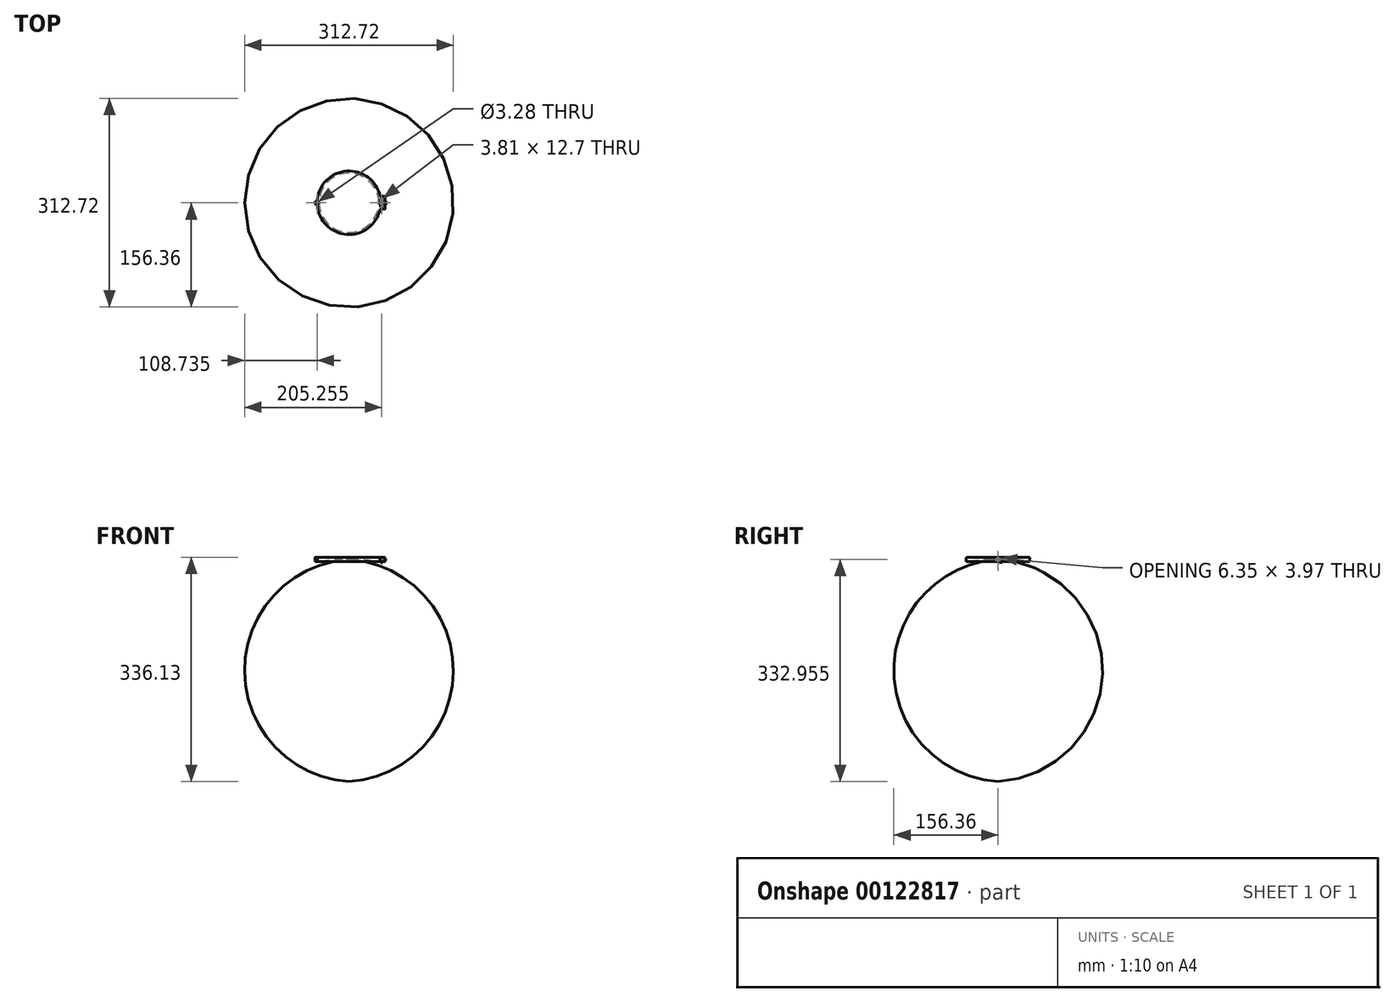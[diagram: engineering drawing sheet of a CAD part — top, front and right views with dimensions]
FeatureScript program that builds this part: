
annotation { "Feature Type Name" : "Feature", "Feature Type Description" : "" }
export const myFeature = defineFeature(function(context is Context, id is Id, definition is map)
    precondition{}
    {
        {
            var Q0;
            Q0=qCreatedBy(makeId("Front.planeOp"),FACE);
            var sketch = newSketch(context, id + "F0", { "sketchPlane" : qUnion([Q0])});
            skLineSegment(sketch, "E0", {"start": v(0, 0) * mm, "end": v(47.63, 0) * mm});
            skLineSegment(sketch, "E1", {"start": v(47.63, 0) * mm, "end": v(47.63, 6.35) * mm});
            skLineSegment(sketch, "E2", {"start": v(47.63, 6.35) * mm, "end": v(44.45, 6.35) * mm});
            skLineSegment(sketch, "E3", {"start": v(44.45, 6.35) * mm, "end": v(44.45, 6.35) * mm});
            skLineSegment(sketch, "E4", {"start": v(0, 3.17) * mm, "end": v(0, 0) * mm});
            skPoint(sketch, "E5.1.internal.snap0", {"position": v(0, 3.17) * mm});
            skArc(sketch, "E6", {"start": v(0, 3.17) * mm, "mid": v(22.33, 3.27) * mm, "end": v(44.45, 6.35) * mm});
            skPoint(sketch, "E7.orphan", {"position": v(0, 6.35) * mm});
            skSolve(sketch);
        }
        {
            var Q0;
            Q0=makeQuery(id+"F0.imprint","IMPRINT",FACE,{"disambiguationData":[TD([[makeQuery(id+"F0.imprint","IMPRINT",EDGE,{"derivedFrom":sQuery(id+"F0.wireOp",EDGE,"E0")}),1.0]])]});
            var Q1;
            Q1=sQuery(id+"F0.wireOp",EDGE,"E4");
            revolve(context, id + "F1", {"entities" : qUnion([Q0]), "axis" : qUnion([Q1]), "revolveType" : RevolveType.FULL});
        }
        {
            var Q0;
            Q0=makeQuery(id+"F1.opRevolve","SWEPT_BODY",BODY,{"disambiguationData":[OSD([sQuery(id+"F0.wireOp",EDGE,"E0"),sQuery(id+"F0.wireOp",EDGE,"E1"),sQuery(id+"F0.wireOp",EDGE,"E2"),sQuery(id+"F0.wireOp",EDGE,"E3"),sQuery(id+"F0.wireOp",EDGE,"8306908f-6550-4d79-8b0d-f81cb6d910f5"),sQuery(id+"F0.wireOp",EDGE,"E4")])]});
            var Q1;
            Q1=qCreatedBy(makeId("Top.planeOp"),FACE);
            mirror(context, id + "F2", {"entities" : qUnion([Q0]), "mirrorPlane" : qUnion([Q1])});
        }
        {
            var Q0;
            Q0=makeQuery(id+"F1.opRevolve","SWEPT_BODY",BODY,{"disambiguationData":[OSD([sQuery(id+"F0.wireOp",EDGE,"E0"),sQuery(id+"F0.wireOp",EDGE,"E1"),sQuery(id+"F0.wireOp",EDGE,"E2"),sQuery(id+"F0.wireOp",EDGE,"E3"),sQuery(id+"F0.wireOp",EDGE,"8306908f-6550-4d79-8b0d-f81cb6d910f5"),sQuery(id+"F0.wireOp",EDGE,"E4")])]});
            deleteBodies(context, id + "F3", {"entities" : qUnion([Q0])});
        }
        {
            var Q0;
            Q0=makeQuery(id+"F2.opPattern","COPY",FACE,{"derivedFrom":makeQuery(id+"F1.opRevolve","SWEPT_FACE",FACE,{"disambiguationData":[OSD([sQuery(id+"F0.wireOp",EDGE,"E0")])]}),"instanceName":"1"});
            var sketch = newSketch(context, id + "F4", { "sketchPlane" : qUnion([Q0])});
            skCircle(sketch, "E8", {"center": v(-47.63, 0) * mm, "radius": 3.18 * mm});
            skSolve(sketch);
        }
        {
            var Q0;
            {var subQ0=sQuery(id+"F4.wireOp",EDGE,"E8");var subQ1=makeQuery(id+"F2.opPattern","COPY",EDGE,{"derivedFrom":makeQuery(id+"F1.opRevolve","SWEPT_EDGE",EDGE,{"disambiguationData":[OSD([sQuery(id+"F0.wireOp",EDGE,"E0"),sQuery(id+"F0.wireOp",EDGE,"E1")])]}),"instanceName":"1"});var subQ2=makeQuery(id+"F4.imprint","INTERSECT",VERTEX,{"disambiguationData":[OD(0.0)],"derivedFrom":[subQ1,subQ0]});Q0=makeQuery(id+"F4.imprint","IMPRINT",FACE,{"disambiguationData":[TD([[makeQuery(id+"F4.imprint","IMPRINT",EDGE,{"disambiguationData":[TD([[subQ2,1.0]])],"derivedFrom":subQ0}),1.0]])]});}
            var Q1;
            Q1=makeQuery(id+"F2.opPattern","COPY",FACE,{"derivedFrom":makeQuery(id+"F1.opRevolve","SWEPT_FACE",FACE,{"disambiguationData":[OSD([sQuery(id+"F0.wireOp",EDGE,"E2")])]}),"instanceName":"1"});
            extrude(context, id + "F5", {"entities" : qUnion([Q0]), "operationType" : NewBodyOperationType.ADD, "endBound" : BoundingType.UP_TO_SURFACE, "oppositeDirection" : true, "endBoundEntityFace" : qUnion([Q1]), "depth" : 25.4 * mm});
        }
        {
            var Q0;
            Q0=qCreatedBy(makeId("Front.planeOp"),FACE);
            var sketch = newSketch(context, id + "F6", { "sketchPlane" : qUnion([Q0])});
            skCircle(sketch, "E9", {"center": v(46.04, -6.35) * mm, "radius": 0.8 * mm});
            skLineSegment(sketch, "E10", {"start": v(45.24, -6.35) * mm, "end": v(46.83, -6.35) * mm});
            skSolve(sketch);
        }
        {
            var Q0;
            {var subQ0=sQuery(id+"F6.wireOp",EDGE,"E10");Q0=makeQuery(id+"F6.imprint","IMPRINT",FACE,{"disambiguationData":[TD([[makeQuery(id+"F6.imprint","IMPRINT",EDGE,{"derivedFrom":subQ0}),-1.0]])]});}
            var Q1;
            Q1=sQuery(id+"F6.wireOp",EDGE,"E10");
            revolve(context, id + "F7", {"operationType" : NewBodyOperationType.REMOVE, "entities" : qUnion([Q0]), "axis" : qUnion([Q1]), "revolveType" : RevolveType.FULL, "oppositeDirection" : true});
        }
        {
            var Q0;
            {var subQ0=sQuery(id+"F0.wireOp",EDGE,"E0");Q0=makeQuery(id+"F5.boolean.opBoolean","MERGE",FACE,{"derivedFrom":[makeQuery(id+"F2.opPattern","COPY",FACE,{"derivedFrom":makeQuery(id+"F1.opRevolve","SWEPT_FACE",FACE,{"disambiguationData":[OSD([subQ0])]}),"instanceName":"1"}),makeQuery(id+"F5.opExtrude","CAP_FACE",FACE,{"disambiguationData":[OSD([subQ0,sQuery(id+"F0.wireOp",EDGE,"E1"),sQuery(id+"F4.wireOp",EDGE,"E8")])],"isStart":true})]});}
            var sketch = newSketch(context, id + "F8", { "sketchPlane" : qUnion([Q0])});
            skPoint(sketch, "E11", {"position": v(-47.63, 0) * mm});
            skSolve(sketch);
        }
        {
            var Q0;
            Q0=sQuery(id+"F8.wireOp",VERTEX,"E11");
            var Q1;
            Q1=makeQuery(id+"F2.opPattern","COPY",BODY,{"derivedFrom":makeQuery(id+"F1.opRevolve","SWEPT_BODY",BODY,{"disambiguationData":[OSD([sQuery(id+"F0.wireOp",EDGE,"E0"),sQuery(id+"F0.wireOp",EDGE,"E1"),sQuery(id+"F0.wireOp",EDGE,"E2"),sQuery(id+"F0.wireOp",EDGE,"E3"),sQuery(id+"F0.wireOp",EDGE,"8306908f-6550-4d79-8b0d-f81cb6d910f5"),sQuery(id+"F0.wireOp",EDGE,"E4")])]}),"instanceName":"1"});
            hole(context, id + "F9", {"style" : HoleStyle.C_SINK, "endStyle" : HoleEndStyle.THROUGH, "holeDiameter" : 3.28 * mm, "cSinkDiameter" : 3.97 * mm, "cSinkAngle" : 90 * degree, "startFromSketch" : true, "locations" : qUnion([Q0]), "scope" : qUnion([Q1]), "isTappedThrough" : true});
        }
        {
            var Q0;
            {var subQ0=sQuery(id+"F0.wireOp",EDGE,"E0");Q0=makeQuery(id+"F5.boolean.opBoolean","MERGE",FACE,{"derivedFrom":[makeQuery(id+"F2.opPattern","COPY",FACE,{"derivedFrom":makeQuery(id+"F1.opRevolve","SWEPT_FACE",FACE,{"disambiguationData":[OSD([subQ0])]}),"instanceName":"1"}),makeQuery(id+"F5.opExtrude","CAP_FACE",FACE,{"disambiguationData":[OSD([subQ0,sQuery(id+"F0.wireOp",EDGE,"E1"),sQuery(id+"F4.wireOp",EDGE,"E8")])],"isStart":true})]});}
            var sketch = newSketch(context, id + "F10", { "sketchPlane" : qUnion([Q0])});
            skLineSegment(sketch, "E12.bottom", {"start": v(53.98, 9.53) * mm, "end": v(41.28, 9.53) * mm});
            skLineSegment(sketch, "E12.top", {"start": v(53.98, -9.52) * mm, "end": v(41.28, -9.52) * mm});
            skLineSegment(sketch, "E12.left", {"start": v(53.98, 9.52) * mm, "end": v(53.98, -9.53) * mm});
            skLineSegment(sketch, "E12.right", {"start": v(41.28, 9.52) * mm, "end": v(41.28, -9.53) * mm});
            skPoint(sketch, "E12.middle", {"position": v(47.63, 0) * mm});
            skLineSegment(sketch, "E13.bottom", {"start": v(50.8, 6.35) * mm, "end": v(47, 6.35) * mm});
            skLineSegment(sketch, "E13.top", {"start": v(50.8, -6.35) * mm, "end": v(47, -6.35) * mm});
            skLineSegment(sketch, "E13.left", {"start": v(50.8, 6.35) * mm, "end": v(50.8, -6.35) * mm});
            skLineSegment(sketch, "E14", {"start": v(47, 6.35) * mm, "end": v(47, -6.35) * mm});
            skPoint(sketch, "E15.orphan", {"position": v(44.45, 6.35) * mm});
            skPoint(sketch, "E16.orphan", {"position": v(44.45, -6.35) * mm});
            skSolve(sketch);
        }
        {
            var Q0;
            {var subQ4=sQuery(id+"F10.wireOp",EDGE,"E12.left");Q0=makeQuery(id+"F10.imprint","IMPRINT",FACE,{"disambiguationData":[TD([[makeQuery(id+"F10.imprint","IMPRINT",EDGE,{"derivedFrom":subQ4}),-1.0]])]});}
            var Q1;
            {var subQ0=sQuery(id+"F0.wireOp",EDGE,"E2");Q1=makeQuery(id+"F5.boolean.opBoolean","MERGE",FACE,{"derivedFrom":[makeQuery(id+"F2.opPattern","COPY",FACE,{"derivedFrom":makeQuery(id+"F1.opRevolve","SWEPT_FACE",FACE,{"disambiguationData":[OSD([subQ0])]}),"instanceName":"1"}),makeQuery(id+"F5.opExtrude","CAP_FACE",FACE,{"disambiguationData":[OSD([subQ0])],"isStart":false})]});}
            extrude(context, id + "F11", {"entities" : qUnion([Q0]), "operationType" : NewBodyOperationType.ADD, "endBound" : BoundingType.UP_TO_SURFACE, "oppositeDirection" : true, "endBoundEntityFace" : qUnion([Q1]), "depth" : 25.4 * mm});
        }
        {
            var Q0;
            {var subQ0=sQuery(id+"F10.wireOp",EDGE,"E14");Q0=makeQuery(id+"F10.imprint","IMPRINT",FACE,{"disambiguationData":[TD([[makeQuery(id+"F10.imprint","IMPRINT",EDGE,{"derivedFrom":subQ0}),1.0]])]});}
            extrude(context, id + "F12", {"entities" : qUnion([Q0]), "operationType" : NewBodyOperationType.REMOVE, "endBound" : BoundingType.THROUGH_ALL, "oppositeDirection" : true, "depth" : 25.4 * mm});
        }
        {
            var Q0;
            Q0=makeQuery(id+"F11.opExtrude","SWEPT_FACE",FACE,{"disambiguationData":[OSD([sQuery(id+"F10.wireOp",EDGE,"E12.left")])]});
            var sketch = newSketch(context, id + "F13", { "sketchPlane" : qUnion([Q0])});
            skLineSegment(sketch, "E17.bottom", {"start": v(-3.18, -1.2) * mm, "end": v(3.17, -1.2) * mm});
            skLineSegment(sketch, "E17.top", {"start": v(-3.18, -5.16) * mm, "end": v(3.17, -5.16) * mm});
            skLineSegment(sketch, "E17.left", {"start": v(-3.18, -1.2) * mm, "end": v(-3.18, -5.16) * mm});
            skLineSegment(sketch, "E17.right", {"start": v(3.17, -1.2) * mm, "end": v(3.17, -5.16) * mm});
            skLineSegment(sketch, "E18", {"start": v(0, 0) * mm, "end": v(0, -6.35) * mm, "construction": true});
            skSolve(sketch);
        }
        {
            var Q0;
            Q0 = qSketchRegion(id + "F13", true);
            var Q1;
            Q1=makeQuery(id+"F11.opExtrude","SWEPT_FACE",FACE,{"disambiguationData":[OSD([sQuery(id+"F10.wireOp",EDGE,"E13.left")])]});
            extrude(context, id + "F14", {"entities" : qUnion([Q0]), "operationType" : NewBodyOperationType.REMOVE, "endBound" : BoundingType.UP_TO_SURFACE, "oppositeDirection" : true, "endBoundEntityFace" : qUnion([Q1]), "depth" : 25.4 * mm});
        }
        {
            var Q0;
            {var subQ0=sQuery(id+"F0.wireOp",EDGE,"E1");var subQ1=sQuery(id+"F0.wireOp",EDGE,"E0");Q0=makeQuery(id+"F11.boolean.opBoolean","MERGE",FACE,{"derivedFrom":[makeQuery(id+"F5.boolean.opBoolean","MERGE",FACE,{"derivedFrom":[makeQuery(id+"F2.opPattern","COPY",FACE,{"derivedFrom":makeQuery(id+"F1.opRevolve","SWEPT_FACE",FACE,{"disambiguationData":[OSD([subQ1])]}),"instanceName":"1"}),makeQuery(id+"F5.opExtrude","CAP_FACE",FACE,{"disambiguationData":[OSD([subQ1,subQ0,sQuery(id+"F4.wireOp",EDGE,"E8")])],"isStart":true})]}),makeQuery(id+"F11.opExtrude","CAP_FACE",FACE,{"disambiguationData":[OSD([subQ1,subQ0,sQuery(id+"F10.wireOp",EDGE,"E12.bottom"),sQuery(id+"F10.wireOp",EDGE,"E12.top"),sQuery(id+"F10.wireOp",EDGE,"E12.left"),sQuery(id+"F10.wireOp",EDGE,"E13.bottom"),sQuery(id+"F10.wireOp",EDGE,"E13.top"),sQuery(id+"F10.wireOp",EDGE,"E13.left")])],"isStart":true})]});}
            cPlane(context, id + "F15", {"entities" : qUnion([Q0]), "cplaneType" : CPlaneType.OFFSET, "offset" : 0 * mm, "width" : 152.4 * mm, "height" : 152.4 * mm});
        }
        {
            var Q0;
            Q0=qCreatedBy(id+"F15.planeOp",FACE);
            var sketch = newSketch(context, id + "F16", { "sketchPlane" : qUnion([Q0])});
            skLineSegment(sketch, "E19.bottom", {"start": v(47.39, -5.95) * mm, "end": v(50.4, -5.95) * mm});
            skLineSegment(sketch, "E19.top", {"start": v(47.39, 5.95) * mm, "end": v(50.4, 5.95) * mm});
            skLineSegment(sketch, "E19.left", {"start": v(47.39, -5.95) * mm, "end": v(47.39, 5.95) * mm});
            skLineSegment(sketch, "E19.right", {"start": v(50.4, -5.95) * mm, "end": v(50.4, 5.95) * mm});
            skSolve(sketch);
        }
        {
            var Q0;
            Q0 = qSketchRegion(id + "F16", true);
            extrude(context, id + "F17", {"entities" : qUnion([Q0]), "oppositeDirection" : true, "depth" : 7.94 * mm});
        }
        {
            var Q0;
            Q0=makeQuery(id+"F17.opExtrude","SWEPT_FACE",FACE,{"disambiguationData":[OSD([sQuery(id+"F16.wireOp",EDGE,"E19.right")])]});
            var sketch = newSketch(context, id + "F18", { "sketchPlane" : qUnion([Q0])});
            skLineSegment(sketch, "E20", {"start": v(-5.95, -5.56) * mm, "end": v(5.95, -7.94) * mm});
            skLineSegment(sketch, "E21", {"start": v(5.95, -7.94) * mm, "end": v(-5.95, -7.94) * mm});
            skLineSegment(sketch, "E22", {"start": v(-5.95, -7.94) * mm, "end": v(-5.95, -5.56) * mm});
            skSolve(sketch);
        }
        {
            var Q0;
            Q0=makeQuery(id+"F18.imprint","IMPRINT",FACE,{"disambiguationData":[TD([[makeQuery(id+"F18.imprint","IMPRINT",EDGE,{"derivedFrom":sQuery(id+"F18.wireOp",EDGE,"E20")}),-1.0]])]});
            var Q1;
            Q1=makeQuery(id+"F17.opExtrude","SWEPT_FACE",FACE,{"disambiguationData":[OSD([sQuery(id+"F16.wireOp",EDGE,"E19.left")])]});
            extrude(context, id + "F19", {"entities" : qUnion([Q0]), "operationType" : NewBodyOperationType.REMOVE, "endBound" : BoundingType.UP_TO_SURFACE, "oppositeDirection" : true, "endBoundEntityFace" : qUnion([Q1]), "depth" : 25.4 * mm});
        }
        {
            var Q0;
            Q0=makeQuery(id+"F17.opExtrude","SWEPT_FACE",FACE,{"disambiguationData":[OSD([sQuery(id+"F16.wireOp",EDGE,"E19.right")])]});
            var sketch = newSketch(context, id + "F20", { "sketchPlane" : qUnion([Q0])});
            skLineSegment(sketch, "E23.bottom", {"start": v(-2.78, -4.65) * mm, "end": v(2.78, -4.65) * mm});
            skLineSegment(sketch, "E23.top", {"start": v(-2.78, -3.06) * mm, "end": v(2.78, -3.06) * mm});
            skLineSegment(sketch, "E23.left", {"start": v(-2.78, -4.65) * mm, "end": v(-2.78, -3.06) * mm});
            skLineSegment(sketch, "E23.right", {"start": v(2.78, -4.65) * mm, "end": v(2.78, -3.06) * mm});
            skSolve(sketch);
        }
        {
            var Q0;
            Q0=makeQuery(id+"F20.imprint","IMPRINT",FACE,{"disambiguationData":[TD([[makeQuery(id+"F20.imprint","IMPRINT",EDGE,{"derivedFrom":sQuery(id+"F20.wireOp",EDGE,"E23.bottom")}),1.0]])]});
            extrude(context, id + "F21", {"entities" : qUnion([Q0]), "operationType" : NewBodyOperationType.ADD, "depth" : 4.76 * mm});
        }
        {
            var Q0;
            Q0=makeQuery(id+"F11.opExtrude","SWEPT_EDGE",EDGE,{"disambiguationData":[OSD([sQuery(id+"F0.wireOp",EDGE,"E0"),sQuery(id+"F0.wireOp",EDGE,"E1"),sQuery(id+"F10.wireOp",EDGE,"E12.top")])]});
            var Q1;
            Q1=makeQuery(id+"F11.opExtrude","SWEPT_EDGE",EDGE,{"disambiguationData":[OSD([sQuery(id+"F10.wireOp",EDGE,"E12.top"),sQuery(id+"F10.wireOp",EDGE,"E12.left")])]});
            var Q2;
            Q2=makeQuery(id+"F11.opExtrude","SWEPT_EDGE",EDGE,{"disambiguationData":[OSD([sQuery(id+"F10.wireOp",EDGE,"E12.bottom"),sQuery(id+"F10.wireOp",EDGE,"E12.left")])]});
            var Q3;
            Q3=makeQuery(id+"F11.opExtrude","SWEPT_EDGE",EDGE,{"disambiguationData":[OSD([sQuery(id+"F0.wireOp",EDGE,"E0"),sQuery(id+"F0.wireOp",EDGE,"E1"),sQuery(id+"F10.wireOp",EDGE,"E12.bottom")])]});
            var Q4;
            {var subQ0=sQuery(id+"F4.wireOp",EDGE,"E8");var subQ1=sQuery(id+"F0.wireOp",EDGE,"E1");var subQ2=sQuery(id+"F0.wireOp",EDGE,"E0");Q4=makeQuery(id+"F5.opExtrude","SWEPT_EDGE",EDGE,{"disambiguationData":[OSD([subQ2,subQ1,subQ0]),TDD([makeQuery(id+"F4.imprint","INTERSECT",VERTEX,{"disambiguationData":[OD(1.0)],"derivedFrom":[makeQuery(id+"F2.opPattern","COPY",EDGE,{"derivedFrom":makeQuery(id+"F1.opRevolve","SWEPT_EDGE",EDGE,{"disambiguationData":[OSD([subQ2,subQ1])]}),"instanceName":"1"}),subQ0]})])]});}
            var Q5;
            {var subQ0=sQuery(id+"F4.wireOp",EDGE,"E8");var subQ1=sQuery(id+"F0.wireOp",EDGE,"E1");var subQ2=sQuery(id+"F0.wireOp",EDGE,"E0");Q5=makeQuery(id+"F5.opExtrude","SWEPT_EDGE",EDGE,{"disambiguationData":[OSD([subQ2,subQ1,subQ0]),TDD([makeQuery(id+"F4.imprint","INTERSECT",VERTEX,{"disambiguationData":[OD(0.0)],"derivedFrom":[makeQuery(id+"F2.opPattern","COPY",EDGE,{"derivedFrom":makeQuery(id+"F1.opRevolve","SWEPT_EDGE",EDGE,{"disambiguationData":[OSD([subQ2,subQ1])]}),"instanceName":"1"}),subQ0]})])]});}
            var Q6;
            {var subQ1=sQuery(id+"F0.wireOp",EDGE,"E1");var subQ2=sQuery(id+"F0.wireOp",EDGE,"E0");var subQ3=sQuery(id+"F10.wireOp",EDGE,"E12.top");Q6=makeQuery(id+"F11.boolean.opBoolean","SPLIT",EDGE,{"disambiguationData":[TD([makeQuery(id+"F11.opExtrude","SWEPT_FACE",FACE,{"disambiguationData":[OSD([subQ3])]})])],"derivedFrom":makeQuery(id+"F2.opPattern","COPY",EDGE,{"derivedFrom":makeQuery(id+"F1.opRevolve","SWEPT_EDGE",EDGE,{"disambiguationData":[OSD([subQ2,subQ1])]}),"instanceName":"1"})});}
            var Q7;
            Q7=makeQuery(id+"F11.opExtrude","CAP_EDGE",EDGE,{"disambiguationData":[OSD([sQuery(id+"F10.wireOp",EDGE,"E12.left")])],"isStart":true});
            var Q8;
            {var subQ0=sQuery(id+"F0.wireOp",EDGE,"E2");Q8=makeQuery(id+"F11.opExtrude","TWEAK_EDGE",EDGE,{"derivedFrom":[makeQuery(id+"F5.boolean.opBoolean","MERGE",FACE,{"derivedFrom":[makeQuery(id+"F2.opPattern","COPY",FACE,{"derivedFrom":makeQuery(id+"F1.opRevolve","SWEPT_FACE",FACE,{"disambiguationData":[OSD([subQ0])]}),"instanceName":"1"}),makeQuery(id+"F5.opExtrude","CAP_FACE",FACE,{"disambiguationData":[OSD([subQ0])],"isStart":false})]}),makeQuery(id+"F10.imprint","IMPRINT",EDGE,{"derivedFrom":sQuery(id+"F10.wireOp",EDGE,"E12.left")})]});}
            var Q9;
            {var subQ0=sQuery(id+"F10.wireOp",EDGE,"E12.top");var subQ1=sQuery(id+"F0.wireOp",EDGE,"E2");Q9=makeQuery(id+"F11.opExtrude","TWEAK_EDGE",EDGE,{"derivedFrom":[makeQuery(id+"F5.boolean.opBoolean","MERGE",FACE,{"derivedFrom":[makeQuery(id+"F2.opPattern","COPY",FACE,{"derivedFrom":makeQuery(id+"F1.opRevolve","SWEPT_FACE",FACE,{"disambiguationData":[OSD([subQ1])]}),"instanceName":"1"}),makeQuery(id+"F5.opExtrude","CAP_FACE",FACE,{"disambiguationData":[OSD([subQ1])],"isStart":false})]}),makeQuery(id+"F10.imprint","IMPRINT",EDGE,{"disambiguationData":[TD([[makeQuery(id+"F10.imprint","INTERSECT",VERTEX,{"derivedFrom":[subQ0,sQuery(id+"F10.wireOp",EDGE,"E12.left")]}),-1.0]])],"derivedFrom":subQ0})]});}
            var Q10;
            Q10=makeQuery(id+"F14.boolean.opBoolean","COPY",EDGE,{"derivedFrom":makeQuery(id+"F14.opExtrude","SWEPT_EDGE",EDGE,{"disambiguationData":[OSD([sQuery(id+"F13.wireOp",EDGE,"E17.bottom"),sQuery(id+"F13.wireOp",EDGE,"E17.right")])]})});
            var Q11;
            Q11=makeQuery(id+"F14.boolean.opBoolean","COPY",EDGE,{"derivedFrom":makeQuery(id+"F14.opExtrude","SWEPT_EDGE",EDGE,{"disambiguationData":[OSD([sQuery(id+"F13.wireOp",EDGE,"E17.bottom"),sQuery(id+"F13.wireOp",EDGE,"E17.left")])]})});
            var Q12;
            Q12=makeQuery(id+"F14.boolean.opBoolean","COPY",EDGE,{"derivedFrom":makeQuery(id+"F14.opExtrude","SWEPT_EDGE",EDGE,{"disambiguationData":[OSD([sQuery(id+"F13.wireOp",EDGE,"E17.top"),sQuery(id+"F13.wireOp",EDGE,"E17.right")])]})});
            var Q13;
            Q13=makeQuery(id+"F14.boolean.opBoolean","COPY",EDGE,{"derivedFrom":makeQuery(id+"F14.opExtrude","SWEPT_EDGE",EDGE,{"disambiguationData":[OSD([sQuery(id+"F13.wireOp",EDGE,"E17.top"),sQuery(id+"F13.wireOp",EDGE,"E17.left")])]})});
            fillet(context, id + "F22", {"entities" : qUnion([Q0, Q1, Q2, Q3, Q4, Q5, Q6, Q7, Q8, Q9, Q10, Q11, Q12, Q13]), "radius" : 0.5 * mm, "tangentPropagation" : true, "allowEdgeOverflow" : false});
        }
    });
